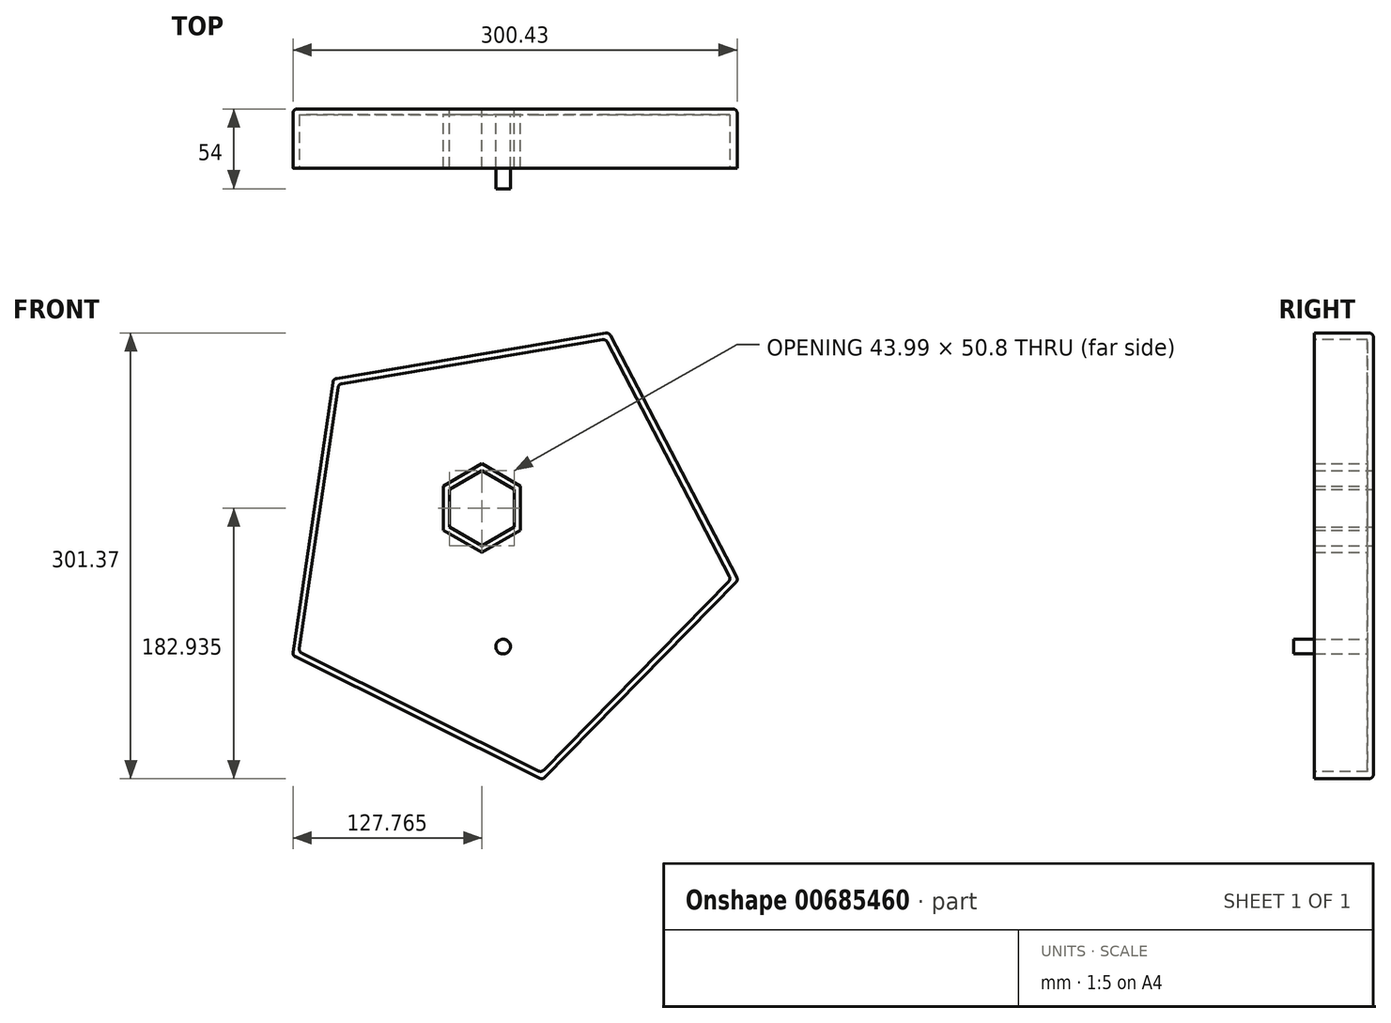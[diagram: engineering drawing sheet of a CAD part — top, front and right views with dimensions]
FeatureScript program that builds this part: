
annotation { "Feature Type Name" : "Feature", "Feature Type Description" : "" }
export const myFeature = defineFeature(function(context is Context, id is Id, definition is map)
    precondition{}
    {
        {
            var Q0;
            Q0=qCreatedBy(makeId("Front.planeOp"),FACE);
            var sketch = newSketch(context, id + "F0", { "sketchPlane" : qUnion([Q0])});
            skCircle(sketch, "E0.cCircle", {"center": v(0, 0) * mm, "radius": 130 * mm, "construction": true});
            skLineSegment(sketch, "E0.0", {"start": v(158.95, -23.56) * mm, "end": v(26.72, -158.45) * mm});
            skLineSegment(sketch, "E0.1", {"start": v(26.72, -158.45) * mm, "end": v(-142.44, -74.37) * mm});
            skLineSegment(sketch, "E0.2", {"start": v(-142.44, -74.37) * mm, "end": v(-114.75, 112.49) * mm});
            skLineSegment(sketch, "E0.3", {"start": v(-114.75, 112.49) * mm, "end": v(71.52, 143.9) * mm});
            skLineSegment(sketch, "E0.4", {"start": v(71.52, 143.9) * mm, "end": v(158.95, -23.56) * mm});
            skPoint(sketch, "E0.0.midPoint", {"position": v(92.83, -91) * mm});
            skLineSegment(sketch, "E1.0", {"start": v(7.61, 37.83) * mm, "end": v(7.61, 12.43) * mm});
            skLineSegment(sketch, "E1.1", {"start": v(7.61, 12.43) * mm, "end": v(-14.38, -0.27) * mm});
            skLineSegment(sketch, "E1.2", {"start": v(-14.38, -0.27) * mm, "end": v(-36.38, 12.43) * mm});
            skLineSegment(sketch, "E1.3", {"start": v(-36.38, 12.43) * mm, "end": v(-36.38, 37.83) * mm});
            skLineSegment(sketch, "E1.4", {"start": v(-36.38, 37.83) * mm, "end": v(-14.38, 50.53) * mm});
            skLineSegment(sketch, "E1.5", {"start": v(-14.38, 50.53) * mm, "end": v(7.61, 37.83) * mm});
            skSolve(sketch);
        }
        {
            var Q0;
            Q0=makeQuery(id+"F0.imprint","IMPRINT",FACE,{"disambiguationData":[TD([[makeQuery(id+"F0.imprint","IMPRINT",EDGE,{"derivedFrom":sQuery(id+"F0.wireOp",EDGE,"E0.0")}),-1.0]])]});
            extrude(context, id + "F1", {"entities" : qUnion([Q0]), "depth" : 40 * mm, "offsetDistance" : 25 * mm});
        }
        {
            var Q0;
            Q0=makeQuery(id+"F1.opExtrude","CAP_FACE",FACE,{"disambiguationData":[OSD([sQuery(id+"F0.wireOp",EDGE,"E0.0"),sQuery(id+"F0.wireOp",EDGE,"E0.1"),sQuery(id+"F0.wireOp",EDGE,"E0.2"),sQuery(id+"F0.wireOp",EDGE,"E0.3"),sQuery(id+"F0.wireOp",EDGE,"E0.4")])],"isStart":false});
            shell(context, id + "F2", {"entities" : qUnion([Q0]), "thickness" : 4 * mm});
        }
        {
            var Q0;
            Q0=makeQuery(id+"F1.opExtrude","CAP_EDGE",EDGE,{"disambiguationData":[OSD([sQuery(id+"F0.wireOp",EDGE,"E0.1")])],"isStart":true});
            var Q1;
            Q1=makeQuery(id+"F1.opExtrude","CAP_EDGE",EDGE,{"disambiguationData":[OSD([sQuery(id+"F0.wireOp",EDGE,"E0.0")])],"isStart":true});
            var Q2;
            Q2=makeQuery(id+"F1.opExtrude","CAP_EDGE",EDGE,{"disambiguationData":[OSD([sQuery(id+"F0.wireOp",EDGE,"E0.2")])],"isStart":true});
            var Q3;
            Q3=makeQuery(id+"F1.opExtrude","CAP_EDGE",EDGE,{"disambiguationData":[OSD([sQuery(id+"F0.wireOp",EDGE,"E0.3")])],"isStart":true});
            var Q4;
            Q4=makeQuery(id+"F1.opExtrude","CAP_EDGE",EDGE,{"disambiguationData":[OSD([sQuery(id+"F0.wireOp",EDGE,"E0.4")])],"isStart":true});
            var Q5;
            Q5=makeQuery(id+"F1.opExtrude","SWEPT_EDGE",EDGE,{"disambiguationData":[OSD([sQuery(id+"F0.wireOp",EDGE,"E0.3"),sQuery(id+"F0.wireOp",EDGE,"E0.4")])]});
            var Q6;
            Q6=makeQuery(id+"F1.opExtrude","SWEPT_EDGE",EDGE,{"disambiguationData":[OSD([sQuery(id+"F0.wireOp",EDGE,"E0.2"),sQuery(id+"F0.wireOp",EDGE,"E0.3")])]});
            var Q7;
            Q7=makeQuery(id+"F1.opExtrude","SWEPT_EDGE",EDGE,{"disambiguationData":[OSD([sQuery(id+"F0.wireOp",EDGE,"E0.1"),sQuery(id+"F0.wireOp",EDGE,"E0.2")])]});
            var Q8;
            Q8=makeQuery(id+"F1.opExtrude","SWEPT_EDGE",EDGE,{"disambiguationData":[OSD([sQuery(id+"F0.wireOp",EDGE,"E0.0"),sQuery(id+"F0.wireOp",EDGE,"E0.1")])]});
            var Q9;
            Q9=makeQuery(id+"F1.opExtrude","SWEPT_EDGE",EDGE,{"disambiguationData":[OSD([sQuery(id+"F0.wireOp",EDGE,"E0.0"),sQuery(id+"F0.wireOp",EDGE,"E0.4")])]});
            var Q10;
            Q10=makeQuery(id+"F2.opShell","OFFSET_EDGE",EDGE,{"disambiguationData":[OSD([sQuery(id+"F0.wireOp",EDGE,"E0.3"),sQuery(id+"F0.wireOp",EDGE,"E0.4")])]});
            var Q11;
            Q11=makeQuery(id+"F2.opShell","OFFSET_EDGE",EDGE,{"disambiguationData":[OSD([sQuery(id+"F0.wireOp",EDGE,"E0.2"),sQuery(id+"F0.wireOp",EDGE,"E0.3")])]});
            var Q12;
            Q12=makeQuery(id+"F2.opShell","OFFSET_EDGE",EDGE,{"disambiguationData":[OSD([sQuery(id+"F0.wireOp",EDGE,"E0.1"),sQuery(id+"F0.wireOp",EDGE,"E0.2")])]});
            var Q13;
            Q13=makeQuery(id+"F2.opShell","OFFSET_EDGE",EDGE,{"disambiguationData":[OSD([sQuery(id+"F0.wireOp",EDGE,"E0.0"),sQuery(id+"F0.wireOp",EDGE,"E0.4")])]});
            var Q14;
            Q14=makeQuery(id+"F2.opShell","OFFSET_EDGE",EDGE,{"disambiguationData":[OSD([sQuery(id+"F0.wireOp",EDGE,"E0.0"),sQuery(id+"F0.wireOp",EDGE,"E0.1")])]});
            fillet(context, id + "F3", {"entities" : qUnion([Q0, Q1, Q2, Q3, Q4, Q5, Q6, Q7, Q8, Q9, Q10, Q11, Q12, Q13, Q14]), "radius" : 3 * mm, "tangentPropagation" : true, "allowEdgeOverflow" : false});
        }
        {
            var Q0;
            {var subQ0=sQuery(id+"F0.wireOp",EDGE,"E1.5");var subQ1=sQuery(id+"F0.wireOp",EDGE,"E1.4");var subQ2=sQuery(id+"F0.wireOp",EDGE,"E1.3");var subQ3=sQuery(id+"F0.wireOp",EDGE,"E1.2");var subQ4=sQuery(id+"F0.wireOp",EDGE,"E1.1");var subQ5=sQuery(id+"F0.wireOp",EDGE,"E1.0");var subQ6=sQuery(id+"F0.wireOp",EDGE,"E0.4");var subQ7=sQuery(id+"F0.wireOp",EDGE,"E0.3");var subQ8=sQuery(id+"F0.wireOp",EDGE,"E0.2");var subQ9=sQuery(id+"F0.wireOp",EDGE,"E0.1");var subQ10=sQuery(id+"F0.wireOp",EDGE,"E0.0");Q0=makeQuery(id+"F2.opShell","OFFSET_FACE",FACE,{"disambiguationData":[OSD([subQ10,subQ9,subQ8,subQ7,subQ6,subQ5,subQ4,subQ3,subQ2,subQ1,subQ0]),TDD([makeQuery(id+"F1.opExtrude","CAP_FACE",FACE,{"disambiguationData":[OSD([subQ10,subQ9,subQ8,subQ7,subQ6,subQ5,subQ4,subQ3,subQ2,subQ1,subQ0])],"isStart":true})])]});}
            var sketch = newSketch(context, id + "F4", { "sketchPlane" : qUnion([Q0])});
            skCircle(sketch, "E2", {"center": v(0, -68.46) * mm, "radius": 5 * mm});
            skSolve(sketch);
        }
        {
            var Q0;
            Q0 = qSketchRegion(id + "F4", true);
            extrude(context, id + "F5", {"entities" : qUnion([Q0]), "operationType" : NewBodyOperationType.ADD, "depth" : 50 * mm, "offsetDistance" : 25 * mm});
        }
    });
